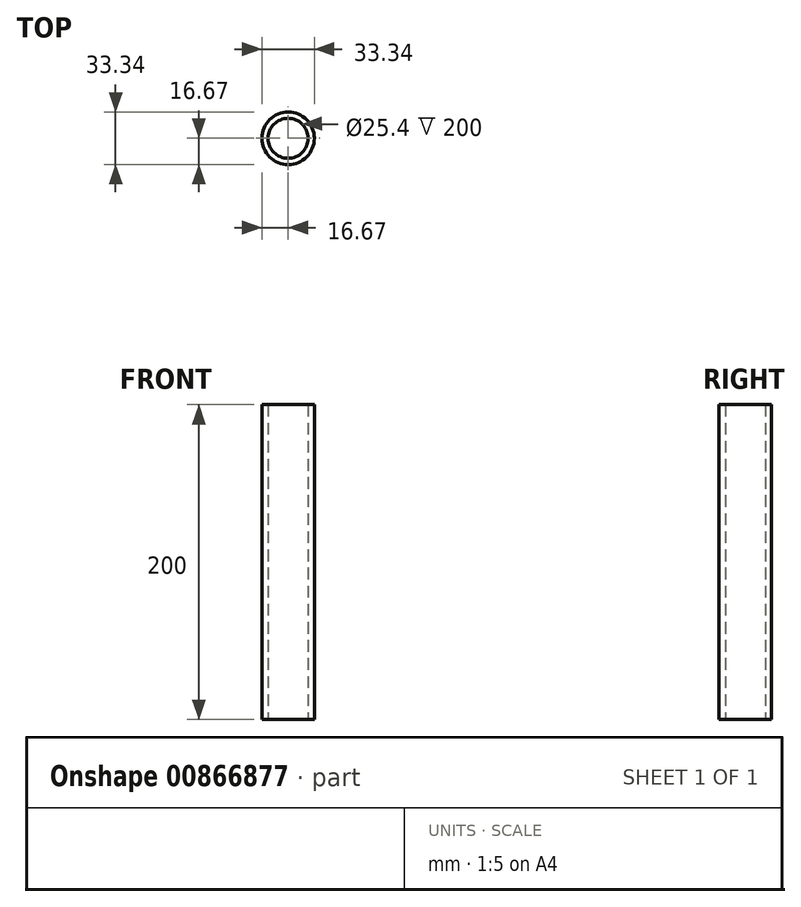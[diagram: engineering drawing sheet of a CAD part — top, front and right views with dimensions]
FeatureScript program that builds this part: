
annotation { "Feature Type Name" : "Feature", "Feature Type Description" : "" }
export const myFeature = defineFeature(function(context is Context, id is Id, definition is map)
    precondition{}
    {
        {
            var Q0;
            Q0=qCreatedBy(makeId("Top.planeOp"),FACE);
            var sketch = newSketch(context, id + "F0", { "sketchPlane" : qUnion([Q0])});
            skCircle(sketch, "E0", {"center": v(0, 0) * mm, "radius": 12.7 * mm});
            skCircle(sketch, "E1", {"center": v(0, 0) * mm, "radius": 16.67 * mm});
            skSolve(sketch);
        }
        {
            var Q0;
            Q0 = qSketchRegion(id + "F0", true);
            extrude(context, id + "F1", {"entities" : qUnion([Q0]), "depth" : 200 * mm, "offsetDistance" : 25.4 * mm});
        }
    });
